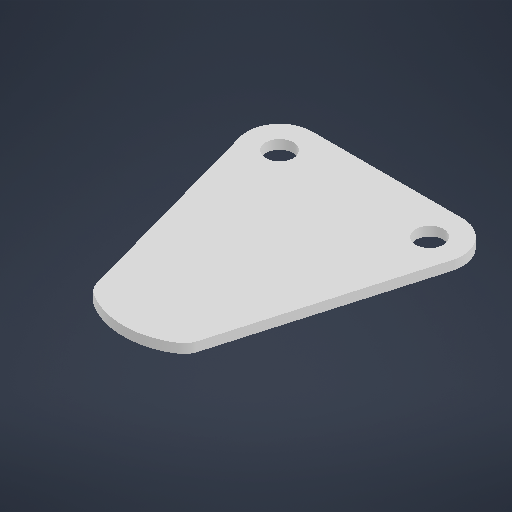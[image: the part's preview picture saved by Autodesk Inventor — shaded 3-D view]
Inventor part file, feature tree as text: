
AUTODESK INVENTOR PART (.ipt)
format: ipt  version: 2025.2 (Build 292293000, 293)  size: 231,936 bytes
history: native  units: in
note: dims shown in document units (in); Inventor stores cm internally (conversion verified against a paired STEP export)
features: other x2, extrude x1, sketch x1
ambient origin geometry x8: Origin, YZ Plane, XZ Plane, XY Plane, X Axis, Y Axis, Z Axis, Center Point
bodies: Solid1 (feature_tree)
feature tree (4):
  extrude  "Extrusion1"  [1 undecoded]
  other  "A-Side Definition"
  sketch  "Sketch1"  dims[d0=0.0625in d1=0.0in]
  other  "Definition1"
note: 1 required parameter value undecoded (feature->parameter linkage not recoverable at this tier; creation-order binding heuristic only, values carry confidence <= 0.55)
